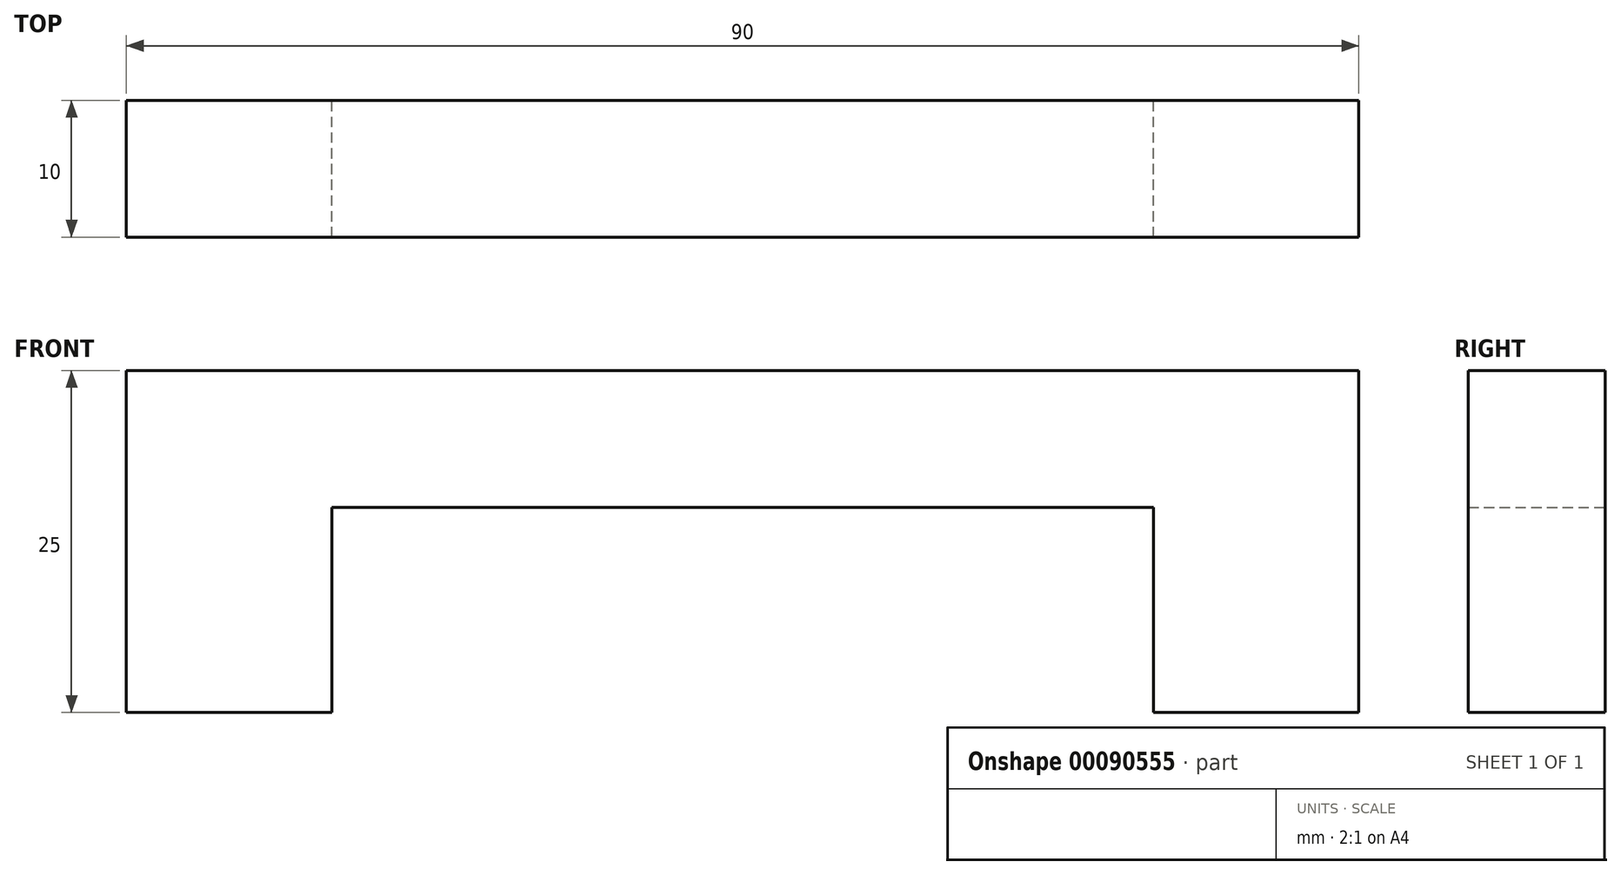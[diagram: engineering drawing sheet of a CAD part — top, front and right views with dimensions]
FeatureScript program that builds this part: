
annotation { "Feature Type Name" : "Feature", "Feature Type Description" : "" }
export const myFeature = defineFeature(function(context is Context, id is Id, definition is map)
    precondition{}
    {
        {
            var Q0;
            Q0=qCreatedBy(makeId("Front.planeOp"),FACE);
            var sketch = newSketch(context, id + "F0", { "sketchPlane" : qUnion([Q0])});
            skLineSegment(sketch, "E0", {"start": v(0, 0) * mm, "end": v(0, 25) * mm});
            skLineSegment(sketch, "E1", {"start": v(0, 25) * mm, "end": v(90, 25) * mm});
            skLineSegment(sketch, "E2", {"start": v(90, 25) * mm, "end": v(90, 0) * mm});
            skLineSegment(sketch, "E3", {"start": v(90, 0) * mm, "end": v(75, 0) * mm});
            skLineSegment(sketch, "E4", {"start": v(75, 0) * mm, "end": v(75, 15) * mm});
            skLineSegment(sketch, "E5", {"start": v(75, 15) * mm, "end": v(15, 15) * mm});
            skLineSegment(sketch, "E6", {"start": v(15, 15) * mm, "end": v(15, 0) * mm});
            skLineSegment(sketch, "E7", {"start": v(15, 0) * mm, "end": v(0, 0) * mm});
            skSolve(sketch);
        }
        {
            var Q0;
            Q0=makeQuery(id+"F0.imprint","IMPRINT",FACE,{"disambiguationData":[TD([[makeQuery(id+"F0.imprint","IMPRINT",EDGE,{"derivedFrom":sQuery(id+"F0.wireOp",EDGE,"E0")}),-1.0]])]});
            extrude(context, id + "F1", {"entities" : qUnion([Q0]), "depth" : 10 * mm});
        }
    });
